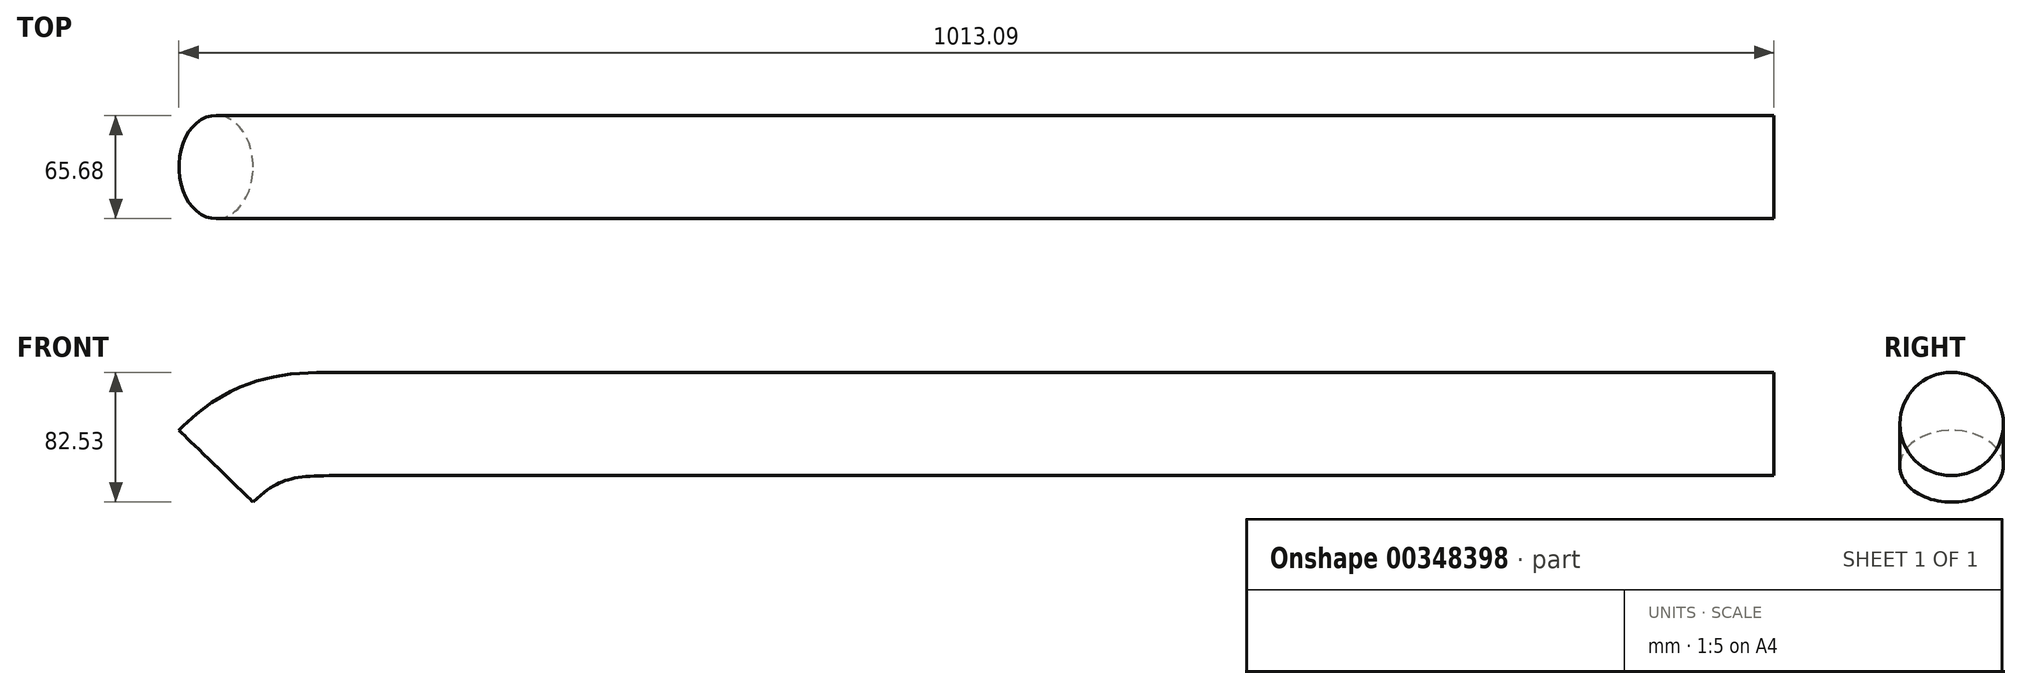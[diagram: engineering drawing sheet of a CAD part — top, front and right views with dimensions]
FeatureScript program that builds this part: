
annotation { "Feature Type Name" : "Feature", "Feature Type Description" : "" }
export const myFeature = defineFeature(function(context is Context, id is Id, definition is map)
    precondition{}
    {
        {
            var Q0;
            Q0=qCreatedBy(makeId("Right.planeOp"),FACE);
            var sketch = newSketch(context, id + "F0", { "sketchPlane" : qUnion([Q0])});
            skCircle(sketch, "E0", {"center": v(0, 0) * mm, "radius": 32.84 * mm});
            skSolve(sketch);
        }
        {
            var Q0;
            Q0=qCreatedBy(makeId("Front.planeOp"),FACE);
            var sketch = newSketch(context, id + "F1", { "sketchPlane" : qUnion([Q0])});
            skFitSpline(sketch, "E1", {"points": [v(-346.52, 0) * mm, v(-425.25, -26.84) * mm], "startDerivative": vector(-83.81, 0) * mm, "endDerivative": vector(-78.03, -80.52) * mm});
            skLineSegment(sketch, "E2", {"start": v(0, 0) * mm, "end": v(-346.52, 0) * mm});
            skSolve(sketch);
        }
        {
            var Q0;
            Q0=makeQuery(id+"F0.imprint","IMPRINT",FACE,{"disambiguationData":[TD([[makeQuery(id+"F0.imprint","IMPRINT",EDGE,{"derivedFrom":sQuery(id+"F0.wireOp",EDGE,"E0")}),1.0]])]});
            var Q1;
            Q1=sQuery(id+"F1.wireOp",EDGE,"E2");
            var Q2;
            Q2=sQuery(id+"F1.wireOp",EDGE,"E1");
            sweep(context, id + "F2", {"profiles" : qUnion([Q0]), "path" : qUnion([Q1, Q2])});
        }
        {
            var Q0;
            Q0=qCreatedBy(makeId("Front.planeOp"),FACE);
            var sketch = newSketch(context, id + "F3", { "sketchPlane" : qUnion([Q0])});
            skLineSegment(sketch, "E3", {"start": v(0, 0) * mm, "end": v(564.25, 0) * mm});
            skSolve(sketch);
        }
        {
            var Q0;
            Q0=makeQuery(id+"F2.opSweep","CAP_FACE",FACE,{"disambiguationData":[OSD([sQuery(id+"F0.wireOp",EDGE,"E0"),sQuery(id+"F1.wireOp",VERTEX,"a8296116-2529-4e09-a280-e8eb4202093c.start")])],"isStart":true});
            var Q1;
            Q1=sQuery(id+"F3.wireOp",EDGE,"E3");
            sweep(context, id + "F4", {"operationType" : NewBodyOperationType.ADD, "profiles" : qUnion([Q0]), "path" : qUnion([Q1])});
        }
    });
